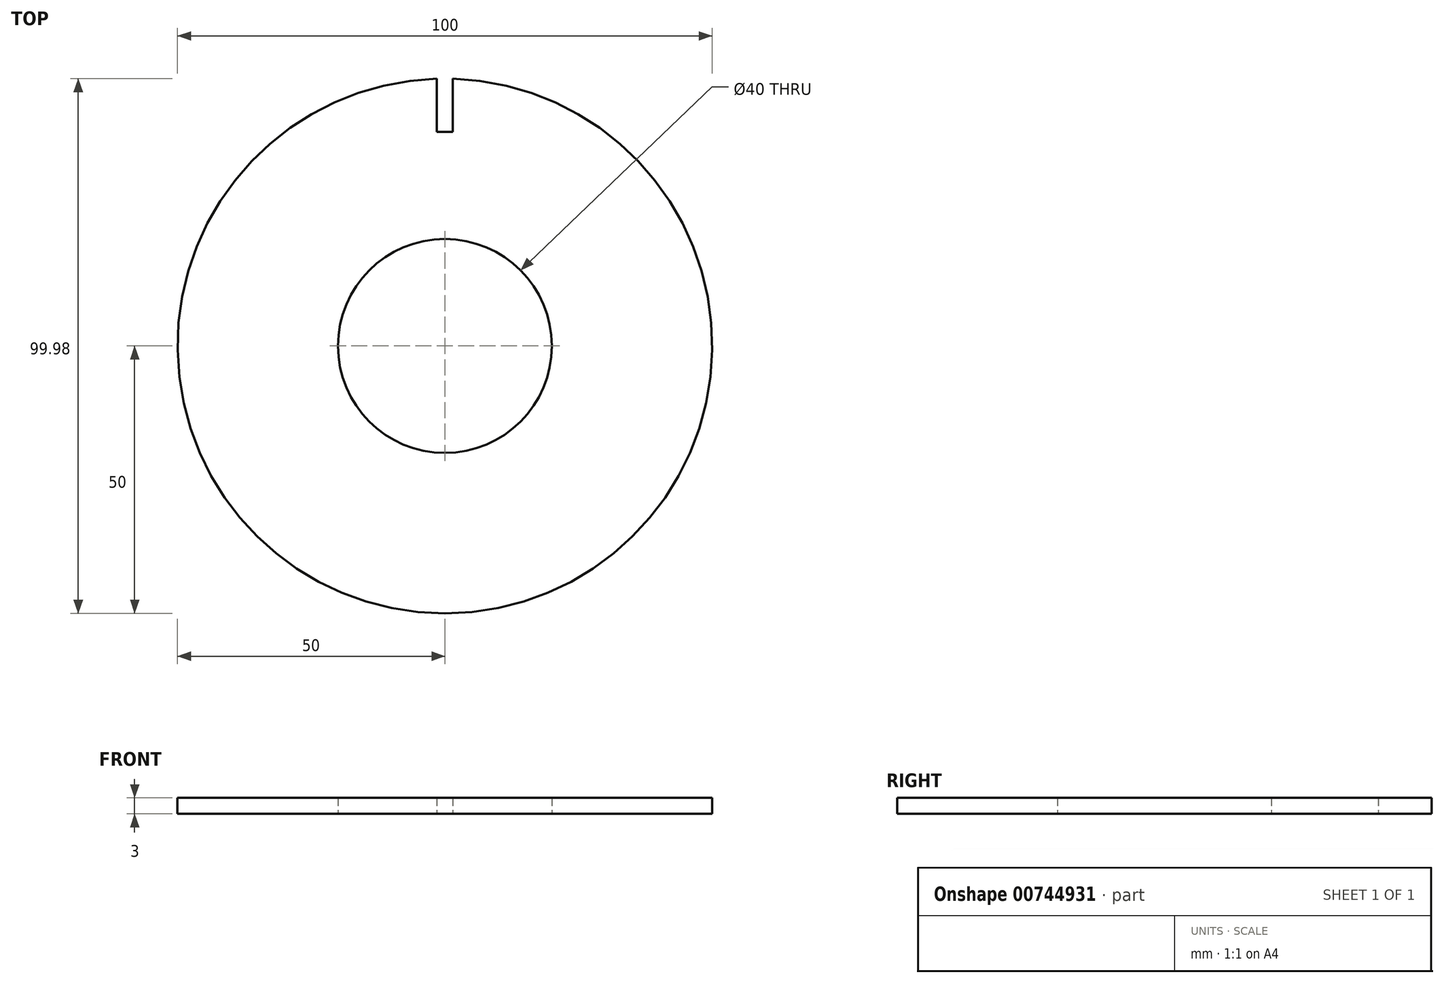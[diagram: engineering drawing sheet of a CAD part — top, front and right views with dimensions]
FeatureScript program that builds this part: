
annotation { "Feature Type Name" : "Feature", "Feature Type Description" : "" }
export const myFeature = defineFeature(function(context is Context, id is Id, definition is map)
    precondition{}
    {
        {
            var Q0;
            Q0=qCreatedBy(makeId("Top.planeOp"),FACE);
            var sketch = newSketch(context, id + "F0", { "sketchPlane" : qUnion([Q0])});
            skCircle(sketch, "E0", {"center": v(0, 0) * mm, "radius": 20 * mm});
            skCircle(sketch, "E1", {"center": v(0, 0) * mm, "radius": 50 * mm});
            skSolve(sketch);
        }
        {
            var Q0;
            Q0=qCreatedBy(makeId("Top.planeOp"),FACE);
            var sketch = newSketch(context, id + "F1", { "sketchPlane" : qUnion([Q0])});
            skLineSegment(sketch, "E2.bottom", {"start": v(-1.5, 50) * mm, "end": v(1.5, 50) * mm});
            skLineSegment(sketch, "E2.top", {"start": v(-1.5, 40) * mm, "end": v(1.5, 40) * mm});
            skLineSegment(sketch, "E2.left", {"start": v(-1.5, 50) * mm, "end": v(-1.5, 40) * mm});
            skLineSegment(sketch, "E2.right", {"start": v(1.5, 50) * mm, "end": v(1.5, 40) * mm});
            skLineSegment(sketch, "E3", {"start": v(0, 40) * mm, "end": v(0, 0) * mm, "construction": true});
            skSolve(sketch);
        }
        {
            var Q0;
            Q0=makeQuery(id+"F0.imprint","IMPRINT",FACE,{"disambiguationData":[TD([[makeQuery(id+"F0.imprint","IMPRINT",EDGE,{"derivedFrom":sQuery(id+"F0.wireOp",EDGE,"E0")}),-1.0]])]});
            extrude(context, id + "F2", {"entities" : qUnion([Q0]), "depth" : 3 * mm, "offsetDistance" : 25 * mm});
        }
        {
            var Q0;
            Q0 = qSketchRegion(id + "F1", true);
            extrude(context, id + "F3", {"entities" : qUnion([Q0]), "operationType" : NewBodyOperationType.REMOVE, "depth" : 25 * mm, "offsetDistance" : 25 * mm});
        }
    });
